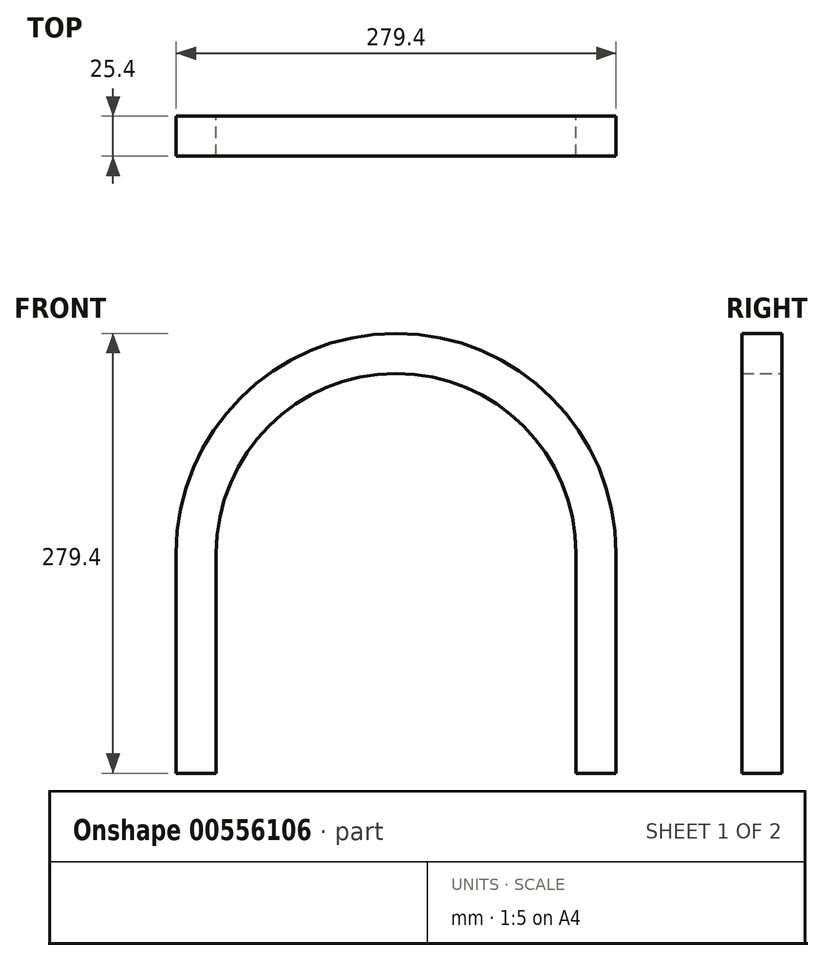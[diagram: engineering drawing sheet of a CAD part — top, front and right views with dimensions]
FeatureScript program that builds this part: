
annotation { "Feature Type Name" : "Feature", "Feature Type Description" : "" }
export const myFeature = defineFeature(function(context is Context, id is Id, definition is map)
    precondition{}
    {
        {
            var Q0;
            Q0=qCreatedBy(makeId("Front.planeOp"),FACE);
            var sketch = newSketch(context, id + "F0", { "sketchPlane" : qUnion([Q0])});
            skArc(sketch, "E0", {"start": v(139.7, 0) * mm, "mid": v(0, 139.7) * mm, "end": v(-139.7, 0) * mm});
            skLineSegment(sketch, "E1", {"start": v(-139.7, 0) * mm, "end": v(-139.7, -139.7) * mm});
            skLineSegment(sketch, "E2", {"start": v(139.7, -139.7) * mm, "end": v(139.7, 0) * mm});
            skArc(sketch, "E3", {"start": v(114.3, 0) * mm, "mid": v(0, 114.3) * mm, "end": v(-114.3, 0) * mm});
            skLineSegment(sketch, "E4", {"start": v(-139.7, -139.7) * mm, "end": v(-114.3, -139.7) * mm});
            skLineSegment(sketch, "E5", {"start": v(-114.3, -139.7) * mm, "end": v(-114.3, 0) * mm});
            skLineSegment(sketch, "E6", {"start": v(139.7, -139.7) * mm, "end": v(114.3, -139.7) * mm});
            skLineSegment(sketch, "E7", {"start": v(114.3, -139.7) * mm, "end": v(114.3, 0) * mm});
            skSolve(sketch);
        }
        {
            var Q0;
            Q0 = qSketchRegion(id + "F0", true);
            extrude(context, id + "F1", {"entities" : qUnion([Q0]), "depth" : 25.4 * mm, "offsetDistance" : 25.4 * mm});
        }
    });
